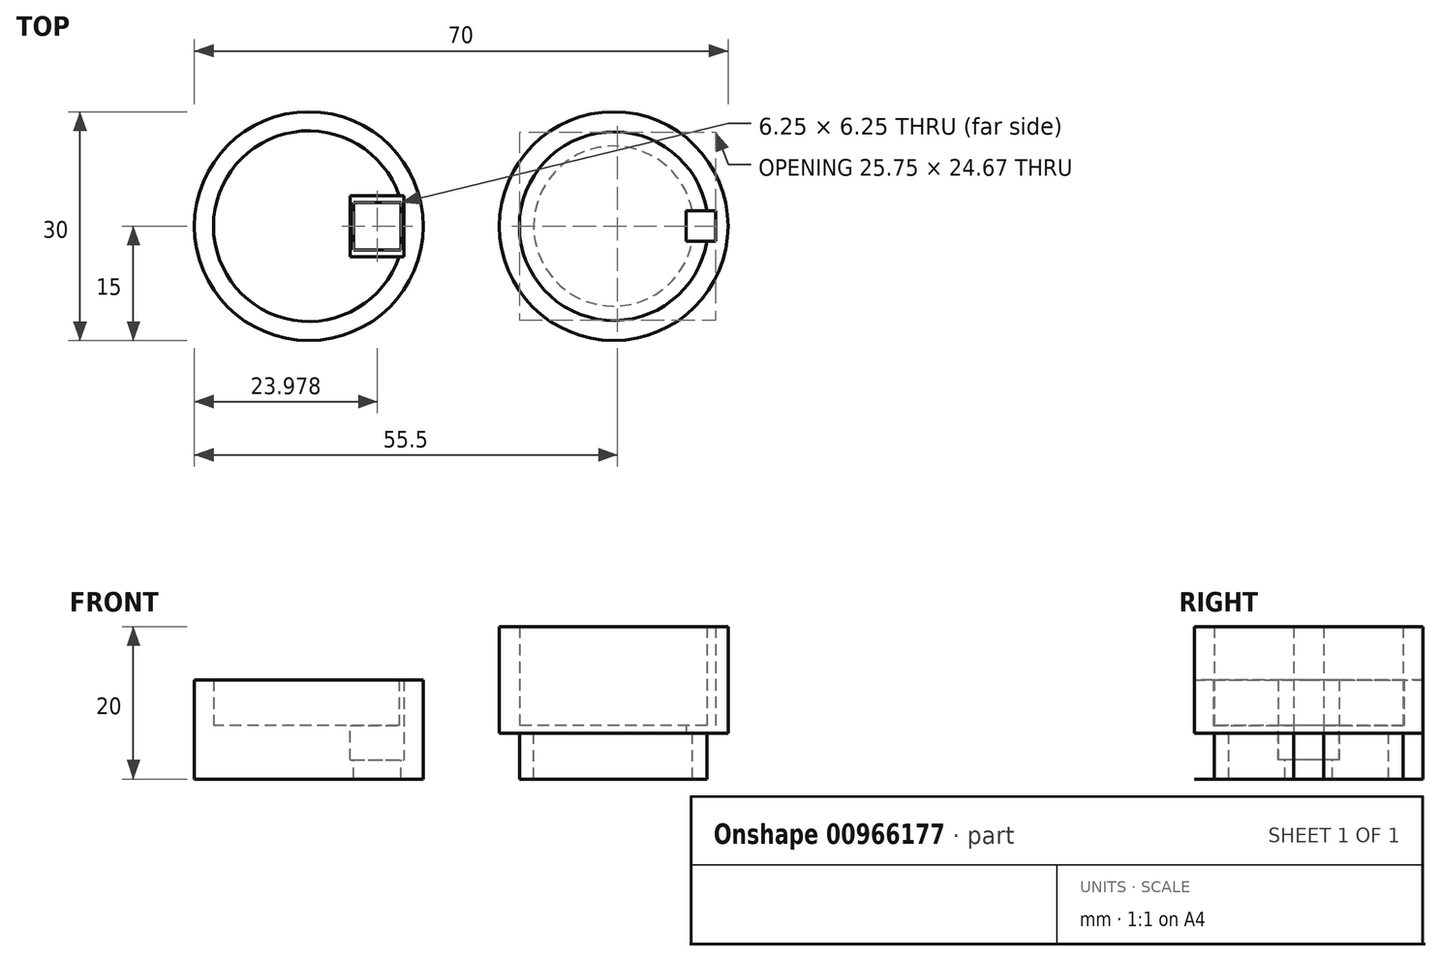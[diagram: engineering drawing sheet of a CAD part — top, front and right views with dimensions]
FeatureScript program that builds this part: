
annotation { "Feature Type Name" : "Feature", "Feature Type Description" : "" }
export const myFeature = defineFeature(function(context is Context, id is Id, definition is map)
    precondition{}
    {
        {
            var Q0;
            Q0=qCreatedBy(makeId("Top.planeOp"),FACE);
            var sketch = newSketch(context, id + "F0", { "sketchPlane" : qUnion([Q0])});
            skCircle(sketch, "E0", {"center": v(0, 0) * mm, "radius": 15 * mm});
            skCircle(sketch, "E1", {"center": v(0, 0) * mm, "radius": 12.38 * mm});
            skCircle(sketch, "E2", {"center": v(0, 0) * mm, "radius": 10.5 * mm});
            skLineSegment(sketch, "E3.bottom", {"start": v(13.38, 2) * mm, "end": v(9.5, 2) * mm});
            skLineSegment(sketch, "E3.top", {"start": v(13.38, -2) * mm, "end": v(9.5, -2) * mm});
            skLineSegment(sketch, "E3.left", {"start": v(13.38, 2) * mm, "end": v(13.38, -2) * mm});
            skLineSegment(sketch, "E3.right", {"start": v(9.5, 2) * mm, "end": v(9.5, -2) * mm});
            skCircle(sketch, "E4", {"center": v(-40, 0) * mm, "radius": 12.5 * mm});
            skCircle(sketch, "E5", {"center": v(-40, 0) * mm, "radius": 15 * mm});
            skLineSegment(sketch, "E6.bottom", {"start": v(-34.15, 3.12) * mm, "end": v(-27.9, 3.12) * mm});
            skLineSegment(sketch, "E6.top", {"start": v(-34.15, -3.12) * mm, "end": v(-27.9, -3.12) * mm});
            skLineSegment(sketch, "E6.left", {"start": v(-34.15, 3.12) * mm, "end": v(-34.15, -3.12) * mm});
            skLineSegment(sketch, "E6.right", {"start": v(-27.9, 3.12) * mm, "end": v(-27.9, -3.12) * mm});
            skPoint(sketch, "E6.middle", {"position": v(-31.02, 0) * mm});
            skLineSegment(sketch, "E7.bottom", {"start": v(-34.54, 4) * mm, "end": v(-27.5, 4) * mm});
            skLineSegment(sketch, "E7.top", {"start": v(-34.54, -4) * mm, "end": v(-27.5, -4) * mm});
            skLineSegment(sketch, "E7.left", {"start": v(-34.54, 4) * mm, "end": v(-34.54, -4) * mm});
            skLineSegment(sketch, "E7.right", {"start": v(-27.5, 4) * mm, "end": v(-27.5, -4) * mm});
            skSolve(sketch);
        }
        {
            var Q0;
            {var subQ0=sQuery(id+"F0.wireOp",EDGE,"E3.bottom");var subQ1=sQuery(id+"F0.wireOp",EDGE,"E1");var subQ2=makeQuery(id+"F0.imprint","INTERSECT",VERTEX,{"derivedFrom":[subQ1,subQ0]});Q0=makeQuery(id+"F0.imprint","IMPRINT",FACE,{"disambiguationData":[TD([[makeQuery(id+"F0.imprint","IMPRINT",EDGE,{"disambiguationData":[TD([[subQ2,-1.0]])],"derivedFrom":subQ1}),1.0]])]});}
            var Q1;
            {var subQ5=sQuery(id+"F0.wireOp",EDGE,"E3.right");Q1=makeQuery(id+"F0.imprint","IMPRINT",FACE,{"disambiguationData":[TD([[makeQuery(id+"F0.imprint","IMPRINT",EDGE,{"derivedFrom":subQ5}),-1.0]])]});}
            extrude(context, id + "F1", {"entities" : qUnion([Q0, Q1]), "depth" : 1 * mm, "offsetDistance" : 25 * mm});
        }
        {
            var Q0;
            Q0=makeQuery(id+"F0.imprint","IMPRINT",FACE,{"disambiguationData":[TD([[makeQuery(id+"F0.imprint","IMPRINT",EDGE,{"derivedFrom":sQuery(id+"F0.wireOp",EDGE,"E0")}),1.0]])]});
            extrude(context, id + "F2", {"entities" : qUnion([Q0]), "operationType" : NewBodyOperationType.ADD, "depth" : 14 * mm, "offsetDistance" : 25 * mm});
        }
        {
            var Q0;
            {var subQ0=sQuery(id+"F0.wireOp",EDGE,"E3.bottom");var subQ1=sQuery(id+"F0.wireOp",EDGE,"E1");var subQ2=makeQuery(id+"F0.imprint","INTERSECT",VERTEX,{"derivedFrom":[subQ1,subQ0]});Q0=makeQuery(id+"F0.imprint","IMPRINT",FACE,{"disambiguationData":[TD([[makeQuery(id+"F0.imprint","IMPRINT",EDGE,{"disambiguationData":[TD([[subQ2,-1.0]])],"derivedFrom":subQ1}),1.0]])]});}
            extrude(context, id + "F3", {"entities" : qUnion([Q0]), "operationType" : NewBodyOperationType.ADD, "oppositeDirection" : true, "depth" : 6 * mm, "offsetDistance" : 25 * mm});
        }
        {
            var Q0;
            Q0=makeQuery(id+"F0.imprint","IMPRINT",FACE,{"disambiguationData":[TD([[makeQuery(id+"F0.imprint","IMPRINT",EDGE,{"derivedFrom":sQuery(id+"F0.wireOp",EDGE,"E5")}),1.0]])]});
            extrude(context, id + "F4", {"entities" : qUnion([Q0]), "depth" : 6 * mm, "offsetDistance" : 25 * mm});
        }
        {
            var Q0;
            Q0=makeQuery(id+"F0.imprint","IMPRINT",FACE,{"disambiguationData":[TD([[makeQuery(id+"F0.imprint","IMPRINT",EDGE,{"derivedFrom":sQuery(id+"F0.wireOp",EDGE,"E5")}),1.0]])]});
            var Q1;
            {var subQ5=sQuery(id+"F0.wireOp",EDGE,"E7.left");Q1=makeQuery(id+"F0.imprint","IMPRINT",FACE,{"disambiguationData":[TD([[makeQuery(id+"F0.imprint","IMPRINT",EDGE,{"derivedFrom":subQ5}),-1.0]])]});}
            extrude(context, id + "F5", {"entities" : qUnion([Q0, Q1]), "operationType" : NewBodyOperationType.ADD, "oppositeDirection" : true, "depth" : 4.5 * mm, "offsetDistance" : 25 * mm});
        }
        {
            var Q0;
            {var subQ5=sQuery(id+"F0.wireOp",EDGE,"E7.left");Q0=makeQuery(id+"F0.imprint","IMPRINT",FACE,{"disambiguationData":[TD([[makeQuery(id+"F0.imprint","IMPRINT",EDGE,{"derivedFrom":subQ5}),-1.0]])]});}
            var Q1;
            {var subQ6=sQuery(id+"F0.wireOp",EDGE,"E6.bottom");Q1=makeQuery(id+"F0.imprint","IMPRINT",FACE,{"disambiguationData":[TD([[makeQuery(id+"F0.imprint","IMPRINT",EDGE,{"derivedFrom":subQ6}),1.0]])]});}
            var Q2;
            {var subQ2=sQuery(id+"F0.wireOp",EDGE,"E7.right");var subQ4=sQuery(id+"F0.wireOp",EDGE,"E7.bottom");var subQ5=makeQuery(id+"F0.imprint","INTERSECT",VERTEX,{"derivedFrom":[subQ4,subQ2]});Q2=makeQuery(id+"F0.imprint","IMPRINT",FACE,{"disambiguationData":[TD([[makeQuery(id+"F0.imprint","IMPRINT",EDGE,{"disambiguationData":[TD([[subQ5,1.0]])],"derivedFrom":subQ4}),-1.0]])]});}
            var Q3;
            {var subQ2=sQuery(id+"F0.wireOp",EDGE,"E7.top");var subQ4=sQuery(id+"F0.wireOp",EDGE,"E7.right");var subQ5=makeQuery(id+"F0.imprint","INTERSECT",VERTEX,{"derivedFrom":[subQ2,subQ4]});Q3=makeQuery(id+"F0.imprint","IMPRINT",FACE,{"disambiguationData":[TD([[makeQuery(id+"F0.imprint","IMPRINT",EDGE,{"disambiguationData":[TD([[subQ5,1.0]])],"derivedFrom":subQ2}),1.0]])]});}
            var Q4;
            {var subQ0=sQuery(id+"F0.wireOp",EDGE,"E6.right");Q4=makeQuery(id+"F0.imprint","IMPRINT",FACE,{"disambiguationData":[TD([[makeQuery(id+"F0.imprint","IMPRINT",EDGE,{"derivedFrom":subQ0}),1.0]])]});}
            var Q5;
            Q5=makeQuery(id+"F0.imprint","IMPRINT",FACE,{"disambiguationData":[TD([[makeQuery(id+"F0.imprint","IMPRINT",EDGE,{"derivedFrom":sQuery(id+"F0.wireOp",EDGE,"E5")}),1.0]])]});
            extrude(context, id + "F6", {"entities" : qUnion([Q0, Q1, Q2, Q3, Q4, Q5]), "operationType" : NewBodyOperationType.ADD, "oppositeDirection" : true, "depth" : 7 * mm, "offsetDistance" : 25 * mm, "hasSecondDirection" : true, "secondDirectionOppositeDirection" : true, "secondDirectionDepth" : 4.5 * mm});
        }
        {
            var Q0;
            Q0=makeQuery(id+"F1.opExtrude","SWEPT_BODY",BODY,{"disambiguationData":[OSD([sQuery(id+"F0.wireOp",EDGE,"E1"),sQuery(id+"F0.wireOp",EDGE,"E3.bottom"),sQuery(id+"F0.wireOp",EDGE,"E3.top"),sQuery(id+"F0.wireOp",EDGE,"E3.right")])]});
            var Q1;
            Q1=sQuery(id+"Ft6isHpZPgduV7f_2.wireOp",EDGE,"B0dV8sUf-t8ab-rqkN-TlGh-4pbxLVJFJZua");
            var Q2;
            Q2=sQuery(id+"Ft6isHpZPgduV7f_2.wireOp",EDGE,"B0dV8sUf-t8ab-rqkN-TlGh-4pbxLVJFJZua");
            transform(context, id + "F7", {"entities" : qUnion([Q0]), "transformType" : TransformType.TRANSLATION_3D, "dx" : 0 * mm, "dy" : 0 * mm, "dz" : -1 * mm, "makeCopy" : false});
        }
    });
